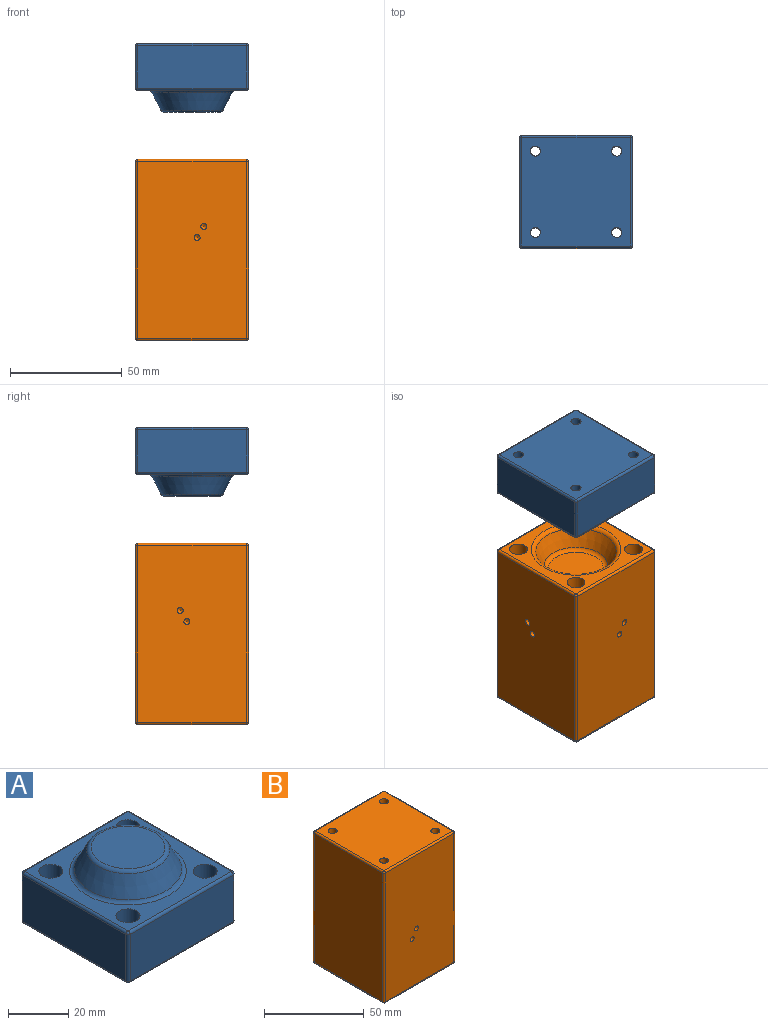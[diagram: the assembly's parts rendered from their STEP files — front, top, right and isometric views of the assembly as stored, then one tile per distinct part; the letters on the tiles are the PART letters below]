
ASSEMBLY  parts=2 mates=1
PART A: 42 faces, bbox 50.5x50.5x30.8 mm
  f0: plane 48.5x19mm, normal (0,1,0), area 921.5mm2, adj f15,f24,f25,f29
  f1: plane 48.5x19mm, normal (-1,0,0), area 921.5mm2, adj f18,f23,f26,f29
  f2: plane 48.5x19mm, normal (0,-1,0), area 921.5mm2, adj f10,f13,f17,f18
  f3: plane 48.5x19mm, normal (1,0,0), area 921.5mm2, adj f10,f14,f15,f16
  f4: plane 48.5x48.5mm, normal (0,0,-1), area 2288.6mm2, adj f13,f14,f23,f24,f30,f33,f36,f39
  f5: plane 48.5x48.5mm, normal (0,0,1), area 963.4mm2, adj f8,f16,f17,f25,f26,f32,f35,f38
  f6: cone r=13.38mm half-angle=27.1deg, axis (0,0,-1), area 879.6mm2, adj f8,f9
  f7: plane 24.61x24.61mm, normal (0,0,1), area 475.7mm2, adj f9
  f8: torus R=19.44mm, axis (0,0,1), area 224.1mm2, adj f5,f6
  f9: torus R=12.31mm, axis (0,0,1), area 158.9mm2, adj f6,f7
  f10: cylinder r=1mm len=19mm, axis (0,0,-1), area 29.8mm2, adj f2,f3,f11,f12
  f11: sphere r=1mm, area 1.6mm2, adj f10,f13,f14
  f12: sphere r=1mm, area 1.6mm2, adj f10,f16,f17
  f13: cylinder r=1mm len=48.5mm, axis (-1,0,0), area 76.2mm2, adj f2,f4,f11,f19
  f14: cylinder r=1mm len=48.5mm, axis (0,-1,0), area 76.2mm2, adj f3,f4,f11,f20
  f15: cylinder r=1mm len=19mm, axis (0,0,1), area 29.8mm2, adj f0,f3,f20,f21
  f16: cylinder r=1mm len=48.5mm, axis (0,1,0), area 76.2mm2, adj f3,f5,f12,f21
  f17: cylinder r=1mm len=48.5mm, axis (1,0,0), area 76.2mm2, adj f2,f5,f12,f22
  f18: cylinder r=1mm len=19mm, axis (0,0,1), area 29.8mm2, adj f1,f2,f19,f22
  f19: sphere r=1mm, area 1.6mm2, adj f13,f18,f23
  f20: sphere r=1mm, area 1.6mm2, adj f14,f15,f24
  f21: sphere r=1mm, area 1.6mm2, adj f15,f16,f25
  f22: sphere r=1mm, area 1.6mm2, adj f17,f18,f26
  f23: cylinder r=1mm len=48.5mm, axis (0,1,0), area 76.2mm2, adj f1,f4,f19,f27
  f24: cylinder r=1mm len=48.5mm, axis (1,0,0), area 76.2mm2, adj f0,f4,f20,f27
  f25: cylinder r=1mm len=48.5mm, axis (-1,0,0), area 76.2mm2, adj f0,f5,f21,f28
  f26: cylinder r=1mm len=48.5mm, axis (0,-1,0), area 76.2mm2, adj f1,f5,f22,f28
  f27: sphere r=1mm, area 1.6mm2, adj f23,f24,f29
  f28: sphere r=1mm, area 1.6mm2, adj f25,f26,f29
  f29: cylinder r=1mm len=19mm, axis (0,0,-1), area 29.8mm2, adj f0,f1,f27,f28
  f30: cylinder r=2.25mm len=4.5mm, axis (0,0,1), area 49.5mm2, adj f4,f31
  f31: plane 8x8mm, normal (0,0,1), area 34.4mm2, adj f30,f32
  f32: cylinder r=4mm len=17.5mm, axis (0,0,1), area 439.8mm2, adj f5,f31
  f33: cylinder r=2.25mm len=4.5mm, axis (0,0,1), area 49.5mm2, adj f4,f34
  f34: plane 8x8mm, normal (0,0,1), area 34.4mm2, adj f33,f35
  f35: cylinder r=4mm len=17.5mm, axis (0,0,1), area 439.8mm2, adj f5,f34
  f36: cylinder r=2.25mm len=4.5mm, axis (0,0,1), area 49.5mm2, adj f4,f37
  f37: plane 8x8mm, normal (0,0,1), area 34.4mm2, adj f36,f38
  f38: cylinder r=4mm len=17.5mm, axis (0,0,1), area 439.8mm2, adj f5,f37
  f39: cylinder r=2.25mm len=4.5mm, axis (0,0,1), area 49.5mm2, adj f4,f40
  f40: plane 8x8mm, normal (0,0,1), area 34.4mm2, adj f39,f41
  f41: cylinder r=4mm len=17.5mm, axis (0,0,1), area 439.8mm2, adj f5,f40
PART B: 50 faces, bbox 50.5x50.5x81 mm
  f0: plane 79x48.5mm, normal (0,1,0), area 3831.5mm2, adj f18,f23,f26,f29
  f1: plane 79x48.5mm, normal (-1,0,0), area 3831.5mm2, adj f15,f24,f25,f29
  f2: plane 79x48.5mm, normal (0,-1,0), area 3820mm2, adj f10,f14,f15,f16,f47,f49
  f3: plane 79x48.5mm, normal (1,0,0), area 3820mm2, adj f10,f13,f17,f18,f43,f45
  f4: plane 48.5x48.5mm, normal (0,0,1), area 2288.6mm2, adj f13,f14,f23,f24,f30,f33,f36,f39
  f5: plane 48.5x48.5mm, normal (0,0,-1), area 890.7mm2, adj f8,f16,f17,f25,f26,f32,f35,f38
  f6: cone r=18.62mm half-angle=26deg, axis (0,0,-1), area 870.6mm2, adj f8,f9
  f7: plane 24.44x24.44mm, normal (0,0,-1), area 469.1mm2, adj f9
  f8: torus R=20.03mm, axis (0,0,1), area 298.4mm2, adj f5,f6
  f9: torus R=12.22mm, axis (0,0,-1), area 210.8mm2, adj f6,f7
  f10: cylinder r=1mm len=79mm, axis (0,0,1), area 124.1mm2, adj f2,f3,f11,f12
  f11: sphere r=1mm, area 1.6mm2, adj f10,f13,f14
  f12: sphere r=1mm, area 1.6mm2, adj f10,f16,f17
  f13: cylinder r=1mm len=48.5mm, axis (0,-1,0), area 76.2mm2, adj f3,f4,f11,f19
  f14: cylinder r=1mm len=48.5mm, axis (-1,0,0), area 76.2mm2, adj f2,f4,f11,f20
  f15: cylinder r=1mm len=79mm, axis (0,0,-1), area 124.1mm2, adj f1,f2,f20,f21
  f16: cylinder r=1mm len=48.5mm, axis (1,0,0), area 76.2mm2, adj f2,f5,f12,f21
  f17: cylinder r=1mm len=48.5mm, axis (0,1,0), area 76.2mm2, adj f3,f5,f12,f22
  f18: cylinder r=1mm len=79mm, axis (0,0,-1), area 124.1mm2, adj f0,f3,f19,f22
  f19: sphere r=1mm, area 1.6mm2, adj f13,f18,f23
  f20: sphere r=1mm, area 1.6mm2, adj f14,f15,f24
  f21: sphere r=1mm, area 1.6mm2, adj f15,f16,f25
  f22: sphere r=1mm, area 1.6mm2, adj f17,f18,f26
  f23: cylinder r=1mm len=48.5mm, axis (1,0,0), area 76.2mm2, adj f0,f4,f19,f27
  f24: cylinder r=1mm len=48.5mm, axis (0,1,0), area 76.2mm2, adj f1,f4,f20,f27
  f25: cylinder r=1mm len=48.5mm, axis (0,-1,0), area 76.2mm2, adj f1,f5,f21,f28
  f26: cylinder r=1mm len=48.5mm, axis (-1,0,0), area 76.2mm2, adj f0,f5,f22,f28
  f27: sphere r=1mm, area 1.6mm2, adj f23,f24,f29
  f28: sphere r=1mm, area 1.6mm2, adj f25,f26,f29
  f29: cylinder r=1mm len=79mm, axis (0,0,1), area 124.1mm2, adj f0,f1,f27,f28
  f30: cylinder r=2.25mm len=4.5mm, axis (0,0,-1), area 49.5mm2, adj f4,f31
  f31: plane 8x8mm, normal (0,0,-1), area 34.4mm2, adj f30,f32
  f32: cylinder r=4mm len=77.5mm, axis (0,0,-1), area 1947.8mm2, adj f5,f31
  f33: cylinder r=2.25mm len=4.5mm, axis (0,0,-1), area 49.5mm2, adj f4,f34
  f34: plane 8x8mm, normal (0,0,-1), area 34.4mm2, adj f33,f35
  f35: cylinder r=4mm len=77.5mm, axis (0,0,-1), area 1947.8mm2, adj f5,f34
  f36: cylinder r=2.25mm len=4.5mm, axis (0,0,-1), area 49.5mm2, adj f4,f37
  f37: plane 8x8mm, normal (0,0,-1), area 34.4mm2, adj f36,f38
  f38: cylinder r=4mm len=77.5mm, axis (0,0,-1), area 1947.8mm2, adj f5,f37
  f39: cylinder r=2.25mm len=4.5mm, axis (0,0,-1), area 49.5mm2, adj f4,f40
  f40: plane 8x8mm, normal (0,0,-1), area 34.4mm2, adj f39,f41
  f41: cylinder r=4mm len=77.5mm, axis (0,0,-1), area 1947.8mm2, adj f5,f40
  f42: cone r=0mm half-angle=59deg, axis (1,0,0), area 6.7mm2, adj f43
  f43: cylinder r=1.35mm len=25mm, axis (1,0,0), area 212.1mm2, adj f3,f42
  f44: cone r=0mm half-angle=59deg, axis (1,0,0), area 6.7mm2, adj f45
  f45: cylinder r=1.35mm len=25mm, axis (1,0,0), area 212.1mm2, adj f3,f44
  f46: cone r=0mm half-angle=59deg, axis (0,-1,0), area 6.7mm2, adj f47
  f47: cylinder r=1.35mm len=25mm, axis (0,-1,0), area 212.1mm2, adj f2,f46
  f48: cone r=0mm half-angle=59deg, axis (0,-1,0), area 6.7mm2, adj f49
  f49: cylinder r=1.35mm len=25mm, axis (0,-1,0), area 212.1mm2, adj f2,f48
PLACE A rot(axis=(0,1,0),180deg) t=(112.52,34.23,160.49)mm
PLACE B rot(axis=(0,1,0),180deg) t=(112.52,34.23,159.73)mm
MATE slider A.f6 <-> B.f6  axis (0,0,1) through (87.27,8.98,180.74)mm
